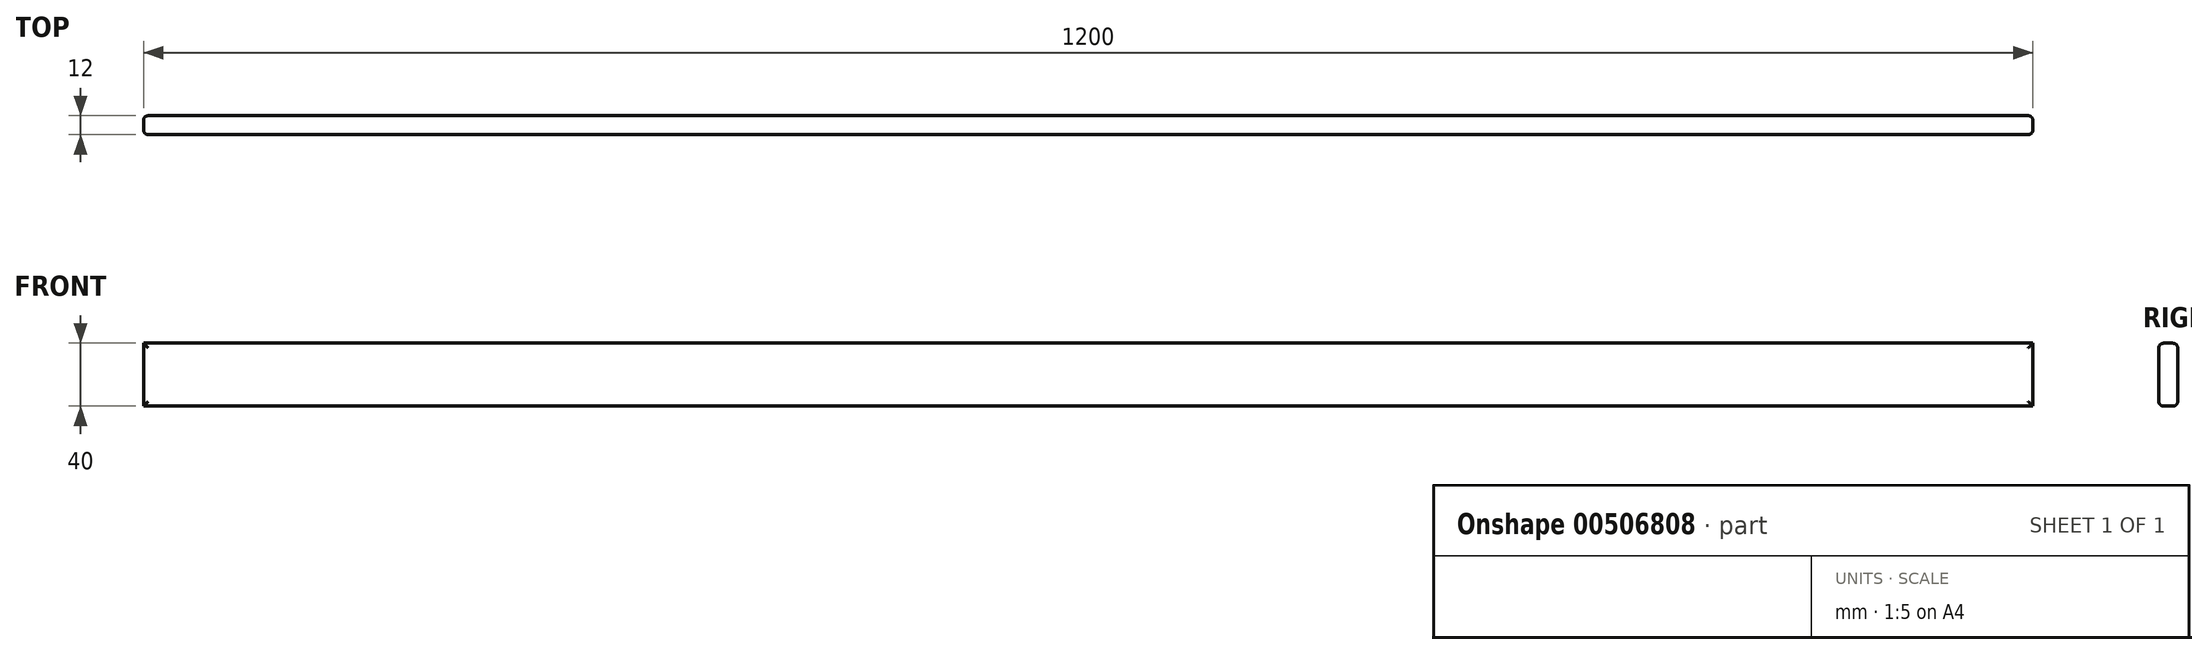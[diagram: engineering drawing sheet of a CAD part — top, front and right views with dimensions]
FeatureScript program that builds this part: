
annotation { "Feature Type Name" : "Feature", "Feature Type Description" : "" }
export const myFeature = defineFeature(function(context is Context, id is Id, definition is map)
    precondition{}
    {
        {
            var Q0;
            Q0=qCreatedBy(makeId("Front.planeOp"),FACE);
            var sketch = newSketch(context, id + "F0", { "sketchPlane" : qUnion([Q0])});
            skLineSegment(sketch, "E0.bottom", {"start": v(-629.35, -2.53) * mm, "end": v(570.65, -2.53) * mm});
            skLineSegment(sketch, "E0.top", {"start": v(-629.35, -42.53) * mm, "end": v(570.65, -42.53) * mm});
            skLineSegment(sketch, "E0.left", {"start": v(-629.35, -2.53) * mm, "end": v(-629.35, -42.53) * mm});
            skLineSegment(sketch, "E0.right", {"start": v(570.65, -2.53) * mm, "end": v(570.65, -42.53) * mm});
            skSolve(sketch);
        }
        {
            var Q0;
            Q0=makeQuery(id+"F0.imprint","IMPRINT",FACE,{"disambiguationData":[TD([[makeQuery(id+"F0.imprint","IMPRINT",EDGE,{"derivedFrom":sQuery(id+"F0.wireOp",EDGE,"E0.bottom")}),-1.0]])]});
            extrude(context, id + "F1", {"entities" : qUnion([Q0]), "depth" : 12 * mm});
        }
        {
            var Q0;
            Q0=makeQuery(id+"F1.opExtrude","SWEPT_FACE",FACE,{"disambiguationData":[OSD([sQuery(id+"F0.wireOp",EDGE,"E0.left")])]});
            var sketch = newSketch(context, id + "F2", { "sketchPlane" : qUnion([Q0])});
            skLineSegment(sketch, "E1", {"start": v(6, -2.53) * mm, "end": v(6, -42.53) * mm});
            skSolve(sketch);
        }
        {
            var Q0;
            Q0=makeQuery(id+"F1.opExtrude","CAP_FACE",FACE,{"disambiguationData":[OSD([sQuery(id+"F0.wireOp",EDGE,"E0.bottom"),sQuery(id+"F0.wireOp",EDGE,"E0.top"),sQuery(id+"F0.wireOp",EDGE,"E0.left"),sQuery(id+"F0.wireOp",EDGE,"E0.right")])],"isStart":false});
            var Q1;
            Q1=makeQuery(id+"F1.opExtrude","CAP_FACE",FACE,{"disambiguationData":[OSD([sQuery(id+"F0.wireOp",EDGE,"E0.bottom"),sQuery(id+"F0.wireOp",EDGE,"E0.top"),sQuery(id+"F0.wireOp",EDGE,"E0.left"),sQuery(id+"F0.wireOp",EDGE,"E0.right")])],"isStart":true});
            fillet(context, id + "F3", {"entities" : qUnion([Q0, Q1]), "radius" : 3 * mm, "tangentPropagation" : true, "allowEdgeOverflow" : false});
        }
    });
